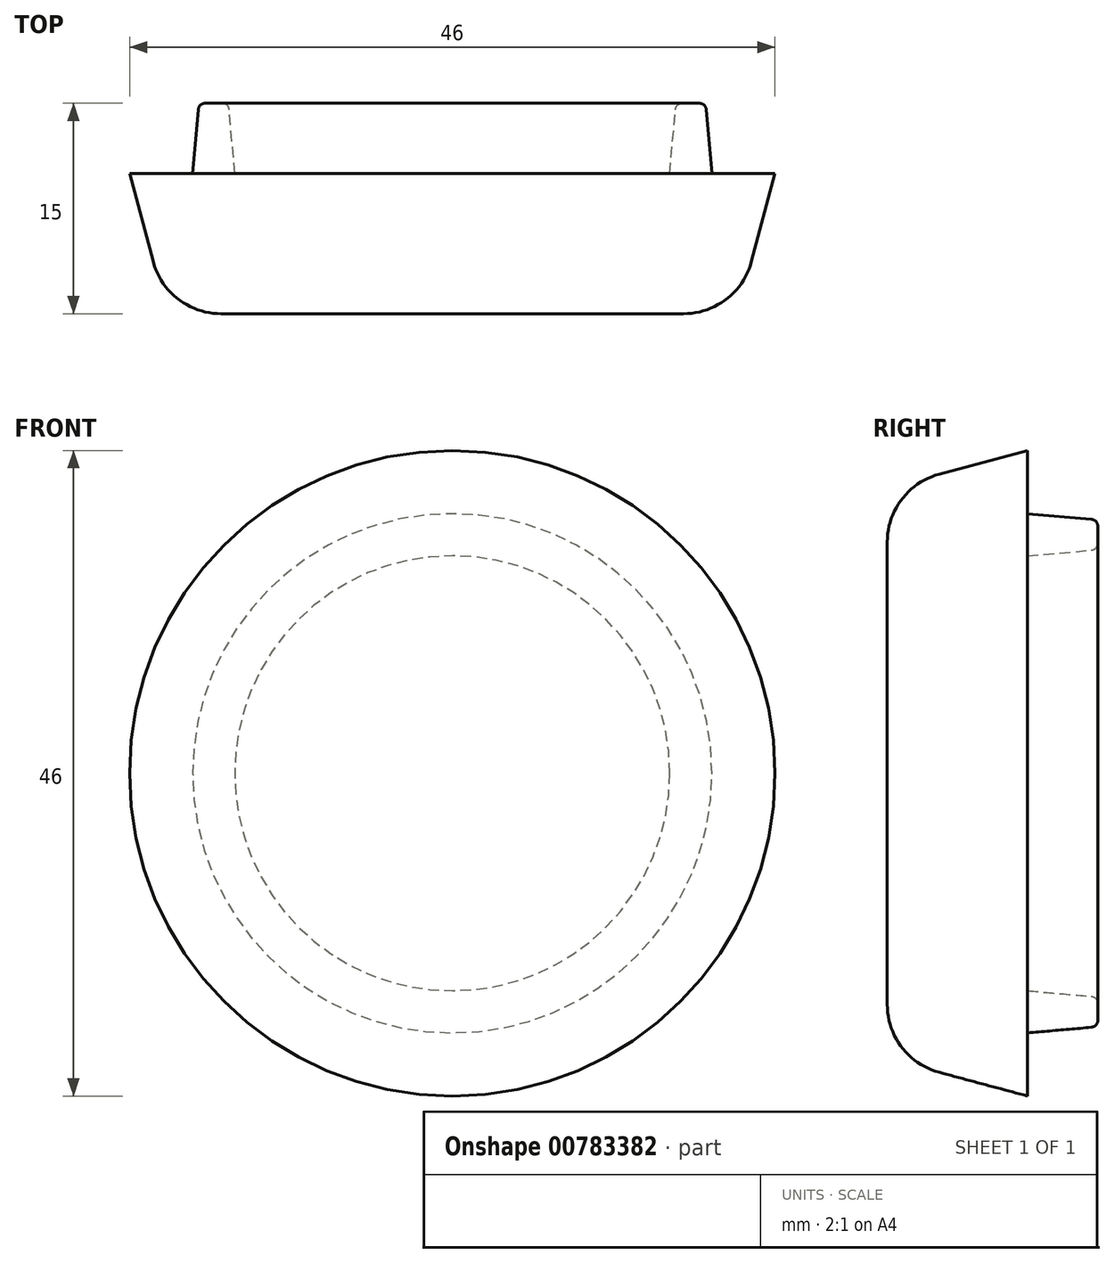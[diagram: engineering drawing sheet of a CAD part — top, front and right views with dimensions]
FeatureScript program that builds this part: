
annotation { "Feature Type Name" : "Feature", "Feature Type Description" : "" }
export const myFeature = defineFeature(function(context is Context, id is Id, definition is map)
    precondition{}
    {
        {
            var Q0;
            Q0=qCreatedBy(makeId("Front.planeOp"),FACE);
            var sketch = newSketch(context, id + "F0", { "sketchPlane" : qUnion([Q0])});
            skCircle(sketch, "E0", {"center": v(0, 0) * mm, "radius": 18.5 * mm});
            skCircle(sketch, "E1", {"center": v(0, 0) * mm, "radius": 23 * mm});
            skCircle(sketch, "E2", {"center": v(0, 0) * mm, "radius": 15.5 * mm});
            skSolve(sketch);
        }
        {
            var Q0;
            Q0=makeQuery(id+"F0.imprint","IMPRINT",FACE,{"disambiguationData":[TD([[makeQuery(id+"F0.imprint","IMPRINT",EDGE,{"derivedFrom":sQuery(id+"F0.wireOp",EDGE,"E0")}),1.0]])]});
            extrude(context, id + "F1", {"entities" : qUnion([Q0]), "oppositeDirection" : true, "depth" : 5 * mm, "offsetDistance" : 25 * mm, "hasDraft" : true, "draftAngle" : 5 * degree, "draftPullDirection" : true});
        }
        {
            var Q0;
            Q0=makeQuery(id+"F0.imprint","IMPRINT",FACE,{"disambiguationData":[TD([[makeQuery(id+"F0.imprint","IMPRINT",EDGE,{"derivedFrom":sQuery(id+"F0.wireOp",EDGE,"E0")}),1.0]])]});
            var Q1;
            Q1=makeQuery(id+"F0.imprint","IMPRINT",FACE,{"disambiguationData":[TD([[makeQuery(id+"F0.imprint","IMPRINT",EDGE,{"derivedFrom":sQuery(id+"F0.wireOp",EDGE,"E0")}),-1.0]])]});
            var Q2;
            Q2=makeQuery(id+"F0.imprint","IMPRINT",FACE,{"disambiguationData":[TD([[makeQuery(id+"F0.imprint","IMPRINT",EDGE,{"derivedFrom":sQuery(id+"F0.wireOp",EDGE,"E2")}),1.0]])]});
            extrude(context, id + "F2", {"entities" : qUnion([Q0, Q1, Q2]), "operationType" : NewBodyOperationType.ADD, "depth" : 10 * mm, "offsetDistance" : 25 * mm, "hasDraft" : true, "draftAngle" : 15 * degree, "draftPullDirection" : true});
        }
        {
            var Q0;
            Q0=makeQuery(id+"F2.opExtrude","CAP_EDGE",EDGE,{"disambiguationData":[OSD([sQuery(id+"F0.wireOp",EDGE,"E1")])],"isStart":false});
            fillet(context, id + "F3", {"entities" : qUnion([Q0]), "radius" : 5 * mm, "tangentPropagation" : true, "allowEdgeOverflow" : false});
        }
        {
            var Q0;
            Q0=makeQuery(id+"F1.opExtrude","CAP_EDGE",EDGE,{"disambiguationData":[OSD([sQuery(id+"F0.wireOp",EDGE,"E0")])],"isStart":false});
            var Q1;
            Q1=makeQuery(id+"F1.opExtrude","CAP_EDGE",EDGE,{"disambiguationData":[OSD([sQuery(id+"F0.wireOp",EDGE,"E2")])],"isStart":false});
            fillet(context, id + "F4", {"entities" : qUnion([Q0, Q1]), "radius" : 0.5 * mm, "tangentPropagation" : true, "allowEdgeOverflow" : false});
        }
    });
